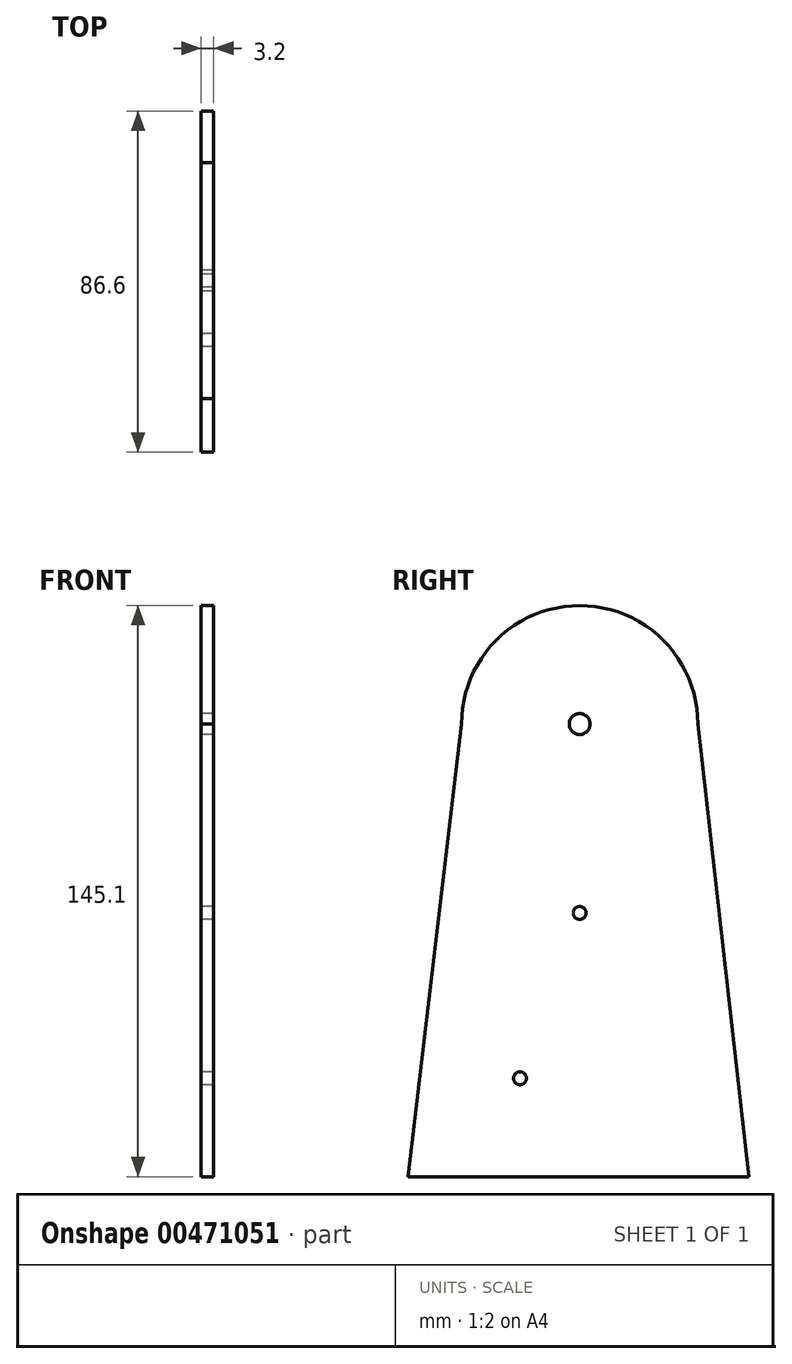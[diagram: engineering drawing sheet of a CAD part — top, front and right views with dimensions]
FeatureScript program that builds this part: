
annotation { "Feature Type Name" : "Feature", "Feature Type Description" : "" }
export const myFeature = defineFeature(function(context is Context, id is Id, definition is map)
    precondition{}
    {
        {
            var Q0;
            Q0=qCreatedBy(makeId("Right.planeOp"),FACE);
            var sketch = newSketch(context, id + "F0", { "sketchPlane" : qUnion([Q0])});
            skLineSegment(sketch, "E0", {"start": v(56.25, 49.09) * mm, "end": v(69.28, -65.91) * mm});
            skLineSegment(sketch, "E1", {"start": v(69.28, -65.91) * mm, "end": v(-17.32, -65.91) * mm});
            skLineSegment(sketch, "E2", {"start": v(-17.32, -65.91) * mm, "end": v(-3.75, 49.09) * mm});
            skCircle(sketch, "E3", {"center": v(26.25, 49.09) * mm, "radius": 2.65 * mm});
            skCircle(sketch, "E4", {"center": v(26.25, 1.09) * mm, "radius": 1.65 * mm});
            skArc(sketch, "E5", {"start": v(56.25, 49.09) * mm, "mid": v(26.25, 79.2) * mm, "end": v(-3.75, 49.09) * mm});
            skCircle(sketch, "E6", {"center": v(11.1, -40.91) * mm, "radius": 1.65 * mm});
            skSolve(sketch);
        }
        {
            var Q0;
            Q0 = qSketchRegion(id + "F0", true);
            extrude(context, id + "F1", {"entities" : qUnion([Q0]), "depth" : 3.2 * mm, "offsetDistance" : 25 * mm});
        }
    });
